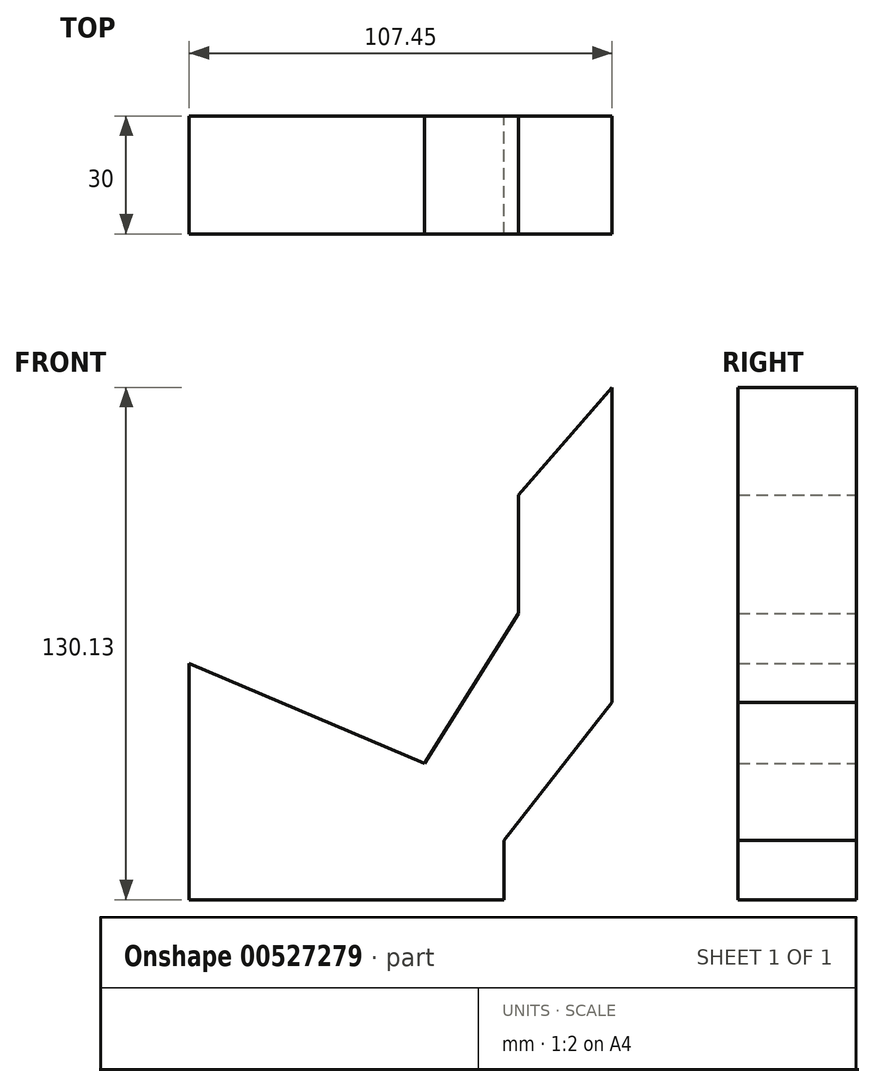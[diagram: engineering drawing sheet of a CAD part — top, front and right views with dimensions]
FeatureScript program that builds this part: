
annotation { "Feature Type Name" : "Feature", "Feature Type Description" : "" }
export const myFeature = defineFeature(function(context is Context, id is Id, definition is map)
    precondition{}
    {
        {
            var Q0;
            Q0=qCreatedBy(makeId("Front.planeOp"),FACE);
            var sketch = newSketch(context, id + "F0", { "sketchPlane" : qUnion([Q0])});
            skLineSegment(sketch, "E0", {"start": v(0, -11.05) * mm, "end": v(-80, -11.05) * mm});
            skLineSegment(sketch, "E1", {"start": v(-80, -11.05) * mm, "end": v(-80, 48.95) * mm});
            skLineSegment(sketch, "E2", {"start": v(-20.17, 23.55) * mm, "end": v(-80, 48.95) * mm});
            skLineSegment(sketch, "E3", {"start": v(0, -11.05) * mm, "end": v(0, 3.95) * mm});
            skLineSegment(sketch, "E4", {"start": v(27.45, 39.08) * mm, "end": v(27.45, 119.08) * mm});
            skLineSegment(sketch, "E5", {"start": v(27.45, 119.08) * mm, "end": v(3.67, 91.72) * mm});
            skLineSegment(sketch, "E6", {"start": v(3.68, 61.72) * mm, "end": v(-20.17, 23.55) * mm});
            skLineSegment(sketch, "E7", {"start": v(3.68, 61.72) * mm, "end": v(3.67, 91.72) * mm});
            skLineSegment(sketch, "E8", {"start": v(0, 3.95) * mm, "end": v(0, 34.24) * mm});
            skLineSegment(sketch, "E9", {"start": v(0, 3.95) * mm, "end": v(27.45, 39.08) * mm});
            skSolve(sketch);
        }
        {
            var Q0;
            Q0 = qSketchRegion(id + "F0", true);
            extrude(context, id + "F1", {"entities" : qUnion([Q0]), "depth" : 30 * mm, "offsetDistance" : 25 * mm});
        }
    });
